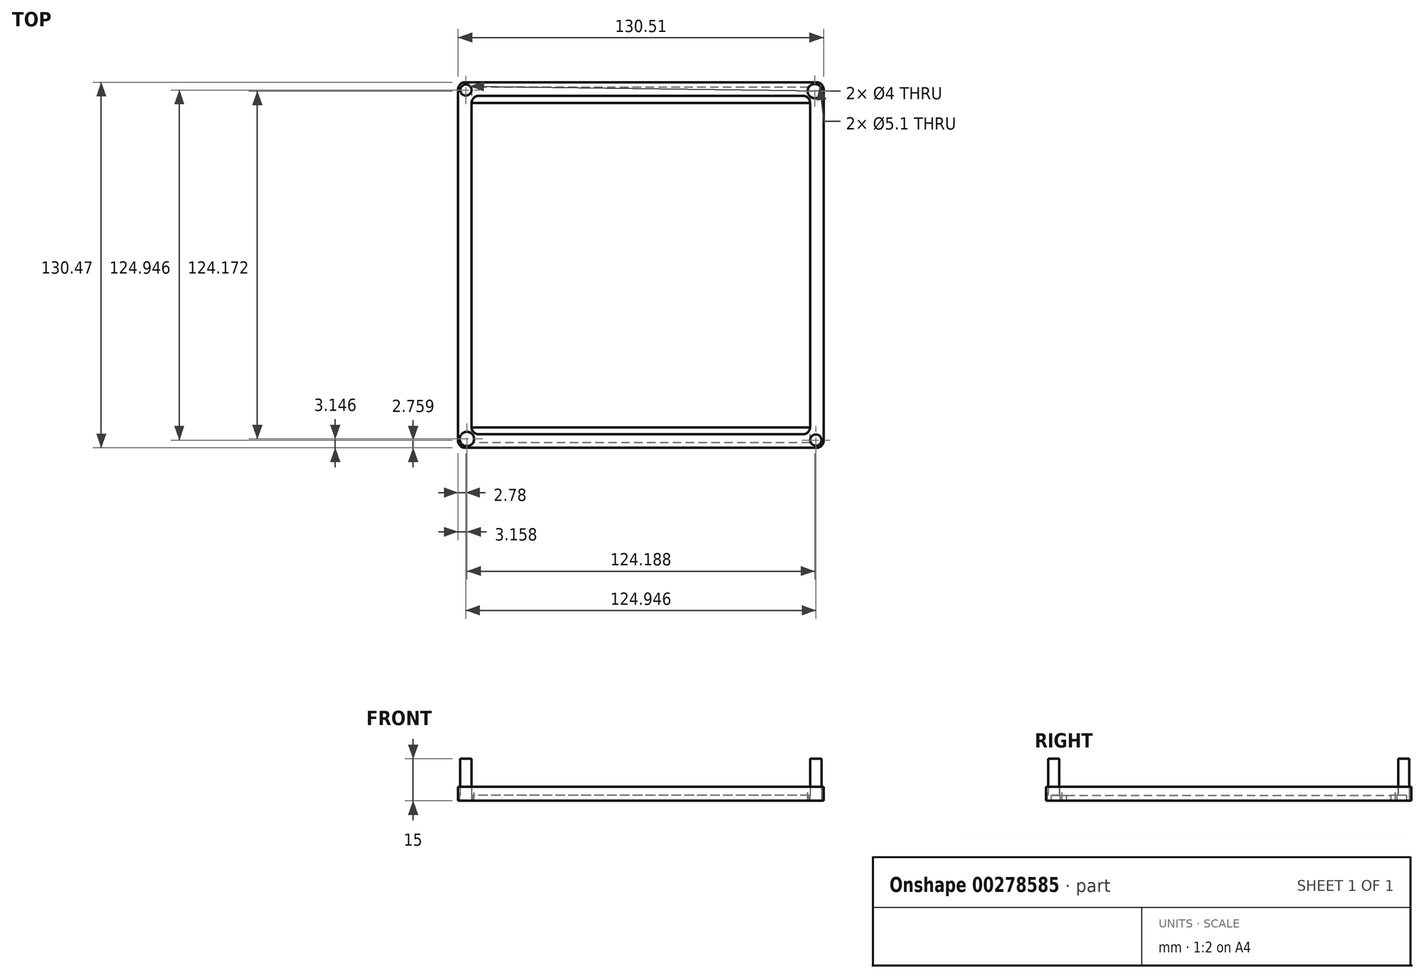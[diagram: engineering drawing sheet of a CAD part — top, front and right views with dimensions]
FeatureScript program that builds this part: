
annotation { "Feature Type Name" : "Feature", "Feature Type Description" : "" }
export const myFeature = defineFeature(function(context is Context, id is Id, definition is map)
    precondition{}
    {
        {
            var Q0;
            Q0=qCreatedBy(makeId("Top.planeOp"),FACE);
            var sketch = newSketch(context, id + "F0", { "sketchPlane" : qUnion([Q0])});
            skCircle(sketch, "E0", {"center": v(-59.38, 76.84) * mm, "radius": 2 * mm});
            skCircle(sketch, "E1", {"center": v(65.57, -48.11) * mm, "radius": 2 * mm});
            skLineSegment(sketch, "E2.bottom", {"start": v(-62.16, 79.6) * mm, "end": v(68.35, 79.6) * mm});
            skLineSegment(sketch, "E2.top", {"start": v(-62.16, -50.87) * mm, "end": v(68.35, -50.87) * mm});
            skLineSegment(sketch, "E2.left", {"start": v(-62.16, 79.6) * mm, "end": v(-62.16, -50.87) * mm});
            skLineSegment(sketch, "E2.right", {"start": v(68.35, 79.6) * mm, "end": v(68.35, -50.87) * mm});
            skPoint(sketch, "E2.middle", {"position": v(3.1, 14.36) * mm});
            skLineSegment(sketch, "E3.bottom", {"start": v(-57.3, 74.76) * mm, "end": v(63.5, 74.76) * mm});
            skLineSegment(sketch, "E3.top", {"start": v(-57.3, -46.04) * mm, "end": v(63.5, -46.04) * mm});
            skLineSegment(sketch, "E3.left", {"start": v(-57.3, 74.76) * mm, "end": v(-57.3, -46.04) * mm});
            skLineSegment(sketch, "E3.right", {"start": v(63.5, 74.76) * mm, "end": v(63.5, -46.04) * mm});
            skSolve(sketch);
        }
        {
            var Q0;
            Q0=makeQuery(id+"F0.imprint","IMPRINT",FACE,{"disambiguationData":[TD([[makeQuery(id+"F0.imprint","IMPRINT",EDGE,{"derivedFrom":sQuery(id+"F0.wireOp",EDGE,"E0")}),1.0]])]});
            extrude(context, id + "F1", {"entities" : qUnion([Q0]), "depth" : 15 * mm});
        }
        {
            var Q0;
            Q0=makeQuery(id+"F0.imprint","IMPRINT",FACE,{"disambiguationData":[TD([[makeQuery(id+"F0.imprint","IMPRINT",EDGE,{"derivedFrom":sQuery(id+"F0.wireOp",EDGE,"E1")}),1.0]])]});
            extrude(context, id + "F2", {"entities" : qUnion([Q0]), "depth" : 15 * mm});
        }
        {
            var Q0;
            Q0=makeQuery(id+"F0.imprint","IMPRINT",FACE,{"disambiguationData":[TD([[makeQuery(id+"F0.imprint","IMPRINT",EDGE,{"derivedFrom":sQuery(id+"F0.wireOp",EDGE,"E0")}),-1.0]])]});
            extrude(context, id + "F3", {"entities" : qUnion([Q0]), "depth" : 5 * mm});
        }
        {
            var Q0;
            Q0=makeQuery(id+"F3.opExtrude","SWEPT_EDGE",EDGE,{"disambiguationData":[OSD([sQuery(id+"F0.wireOp",EDGE,"E2.bottom"),sQuery(id+"F0.wireOp",EDGE,"E2.left")])]});
            fillet(context, id + "F4", {"entities" : qUnion([Q0]), "radius" : 2.5 * mm, "tangentPropagation" : true, "allowEdgeOverflow" : false});
        }
        {
            var Q0;
            Q0=makeQuery(id+"F3.opExtrude","SWEPT_EDGE",EDGE,{"disambiguationData":[OSD([sQuery(id+"F0.wireOp",EDGE,"E3.bottom"),sQuery(id+"F0.wireOp",EDGE,"E3.left")])]});
            fillet(context, id + "F5", {"entities" : qUnion([Q0]), "radius" : 2.5 * mm, "tangentPropagation" : true, "allowEdgeOverflow" : false});
        }
        {
            var Q0;
            Q0=makeQuery(id+"F3.opExtrude","SWEPT_EDGE",EDGE,{"disambiguationData":[OSD([sQuery(id+"F0.wireOp",EDGE,"E3.bottom"),sQuery(id+"F0.wireOp",EDGE,"E3.right")])]});
            var Q1;
            Q1=makeQuery(id+"F3.opExtrude","SWEPT_EDGE",EDGE,{"disambiguationData":[OSD([sQuery(id+"F0.wireOp",EDGE,"E3.top"),sQuery(id+"F0.wireOp",EDGE,"E3.right")])]});
            var Q2;
            Q2=makeQuery(id+"F3.opExtrude","SWEPT_EDGE",EDGE,{"disambiguationData":[OSD([sQuery(id+"F0.wireOp",EDGE,"E3.top"),sQuery(id+"F0.wireOp",EDGE,"E3.left")])]});
            fillet(context, id + "F6", {"entities" : qUnion([Q0, Q1, Q2]), "radius" : 2.5 * mm, "tangentPropagation" : true, "allowEdgeOverflow" : false});
        }
        {
            var Q0;
            Q0=makeQuery(id+"F3.opExtrude","SWEPT_EDGE",EDGE,{"disambiguationData":[OSD([sQuery(id+"F0.wireOp",EDGE,"E2.bottom"),sQuery(id+"F0.wireOp",EDGE,"E2.right")])]});
            var Q1;
            Q1=makeQuery(id+"F3.opExtrude","SWEPT_EDGE",EDGE,{"disambiguationData":[OSD([sQuery(id+"F0.wireOp",EDGE,"E2.top"),sQuery(id+"F0.wireOp",EDGE,"E2.right")])]});
            var Q2;
            Q2=makeQuery(id+"F3.opExtrude","SWEPT_EDGE",EDGE,{"disambiguationData":[OSD([sQuery(id+"F0.wireOp",EDGE,"E2.top"),sQuery(id+"F0.wireOp",EDGE,"E2.left")])]});
            fillet(context, id + "F7", {"entities" : qUnion([Q0, Q1, Q2]), "radius" : 2.5 * mm, "tangentPropagation" : true, "allowEdgeOverflow" : false});
        }
        {
            var Q0;
            Q0=makeQuery(id+"F3.opExtrude","SWEPT_FACE",FACE,{"disambiguationData":[OSD([sQuery(id+"F0.wireOp",EDGE,"E3.left")])]});
            var sketch = newSketch(context, id + "F8", { "sketchPlane" : qUnion([Q0])});
            skLineSegment(sketch, "E4", {"start": v(-43.54, 2) * mm, "end": v(72.26, 2) * mm});
            skSolve(sketch);
        }
        {
            var Q0;
            {var subQ0=sQuery(id+"F8.wireOp",EDGE,"E4");Q0=makeQuery(id+"F8.imprint","IMPRINT",FACE,{"disambiguationData":[TD([[makeQuery(id+"F8.imprint","IMPRINT",EDGE,{"derivedFrom":subQ0}),-1.0]])]});}
            extrude(context, id + "F9", {"entities" : qUnion([Q0]), "operationType" : NewBodyOperationType.ADD, "depth" : 123.1 * mm});
        }
        {
            var Q0;
            Q0=makeQuery(id+"F9.opExtrude","SWEPT_FACE",FACE,{"disambiguationData":[OSD([sQuery(id+"F0.wireOp",EDGE,"E3.bottom"),sQuery(id+"F0.wireOp",EDGE,"E3.left")])]});
            extrude(context, id + "F10", {"entities" : qUnion([Q0]), "depth" : 5.5 * mm});
        }
        {
            var Q0;
            Q0=makeQuery(id+"F9.opExtrude","SWEPT_FACE",FACE,{"disambiguationData":[OSD([sQuery(id+"F0.wireOp",EDGE,"E3.top"),sQuery(id+"F0.wireOp",EDGE,"E3.left")])]});
            extrude(context, id + "F11", {"entities" : qUnion([Q0]), "depth" : 5.5 * mm});
        }
        {
            var Q0;
            Q0=makeQuery(id+"F3.opExtrude","CAP_FACE",FACE,{"disambiguationData":[OSD([sQuery(id+"F0.wireOp",EDGE,"E0"),sQuery(id+"F0.wireOp",EDGE,"E1"),sQuery(id+"F0.wireOp",EDGE,"E2.bottom"),sQuery(id+"F0.wireOp",EDGE,"E2.top"),sQuery(id+"F0.wireOp",EDGE,"E2.left"),sQuery(id+"F0.wireOp",EDGE,"E2.right"),sQuery(id+"F0.wireOp",EDGE,"E3.bottom"),sQuery(id+"F0.wireOp",EDGE,"E3.top"),sQuery(id+"F0.wireOp",EDGE,"E3.left"),sQuery(id+"F0.wireOp",EDGE,"E3.right")])],"isStart":false});
            var sketch = newSketch(context, id + "F12", { "sketchPlane" : qUnion([Q0])});
            skCircle(sketch, "E5", {"center": v(65.19, 76.45) * mm, "radius": 2.55 * mm});
            skLineSegment(sketch, "E6", {"start": v(67.61, 78.87) * mm, "end": v(62.76, 74.03) * mm, "construction": true});
            skSolve(sketch);
        }
        {
            var Q0;
            Q0=makeQuery(id+"F12.imprint","IMPRINT",FACE,{"disambiguationData":[TD([[makeQuery(id+"F12.imprint","IMPRINT",EDGE,{"derivedFrom":sQuery(id+"F12.wireOp",EDGE,"E5")}),1.0]])]});
            extrude(context, id + "F13", {"entities" : qUnion([Q0]), "operationType" : NewBodyOperationType.REMOVE, "oppositeDirection" : true, "offsetDistance" : 25 * mm, "depth" : 10 * mm});
        }
        {
            var Q0;
            Q0=makeQuery(id+"F3.opExtrude","CAP_FACE",FACE,{"disambiguationData":[OSD([sQuery(id+"F0.wireOp",EDGE,"E0"),sQuery(id+"F0.wireOp",EDGE,"E1"),sQuery(id+"F0.wireOp",EDGE,"E2.bottom"),sQuery(id+"F0.wireOp",EDGE,"E2.top"),sQuery(id+"F0.wireOp",EDGE,"E2.left"),sQuery(id+"F0.wireOp",EDGE,"E2.right"),sQuery(id+"F0.wireOp",EDGE,"E3.bottom"),sQuery(id+"F0.wireOp",EDGE,"E3.top"),sQuery(id+"F0.wireOp",EDGE,"E3.left"),sQuery(id+"F0.wireOp",EDGE,"E3.right")])],"isStart":false});
            var sketch = newSketch(context, id + "F14", { "sketchPlane" : qUnion([Q0])});
            skCircle(sketch, "E7", {"center": v(-59, -47.72) * mm, "radius": 2.55 * mm});
            skLineSegment(sketch, "E8", {"start": v(-56.58, -45.3) * mm, "end": v(-61.43, -50.14) * mm, "construction": true});
            skSolve(sketch);
        }
        {
            var Q0;
            Q0=makeQuery(id+"F14.imprint","IMPRINT",FACE,{"disambiguationData":[TD([[makeQuery(id+"F14.imprint","IMPRINT",EDGE,{"derivedFrom":sQuery(id+"F14.wireOp",EDGE,"E7")}),1.0]])]});
            extrude(context, id + "F15", {"entities" : qUnion([Q0]), "operationType" : NewBodyOperationType.REMOVE, "oppositeDirection" : true, "offsetDistance" : 25 * mm, "depth" : 10 * mm});
        }
    });
